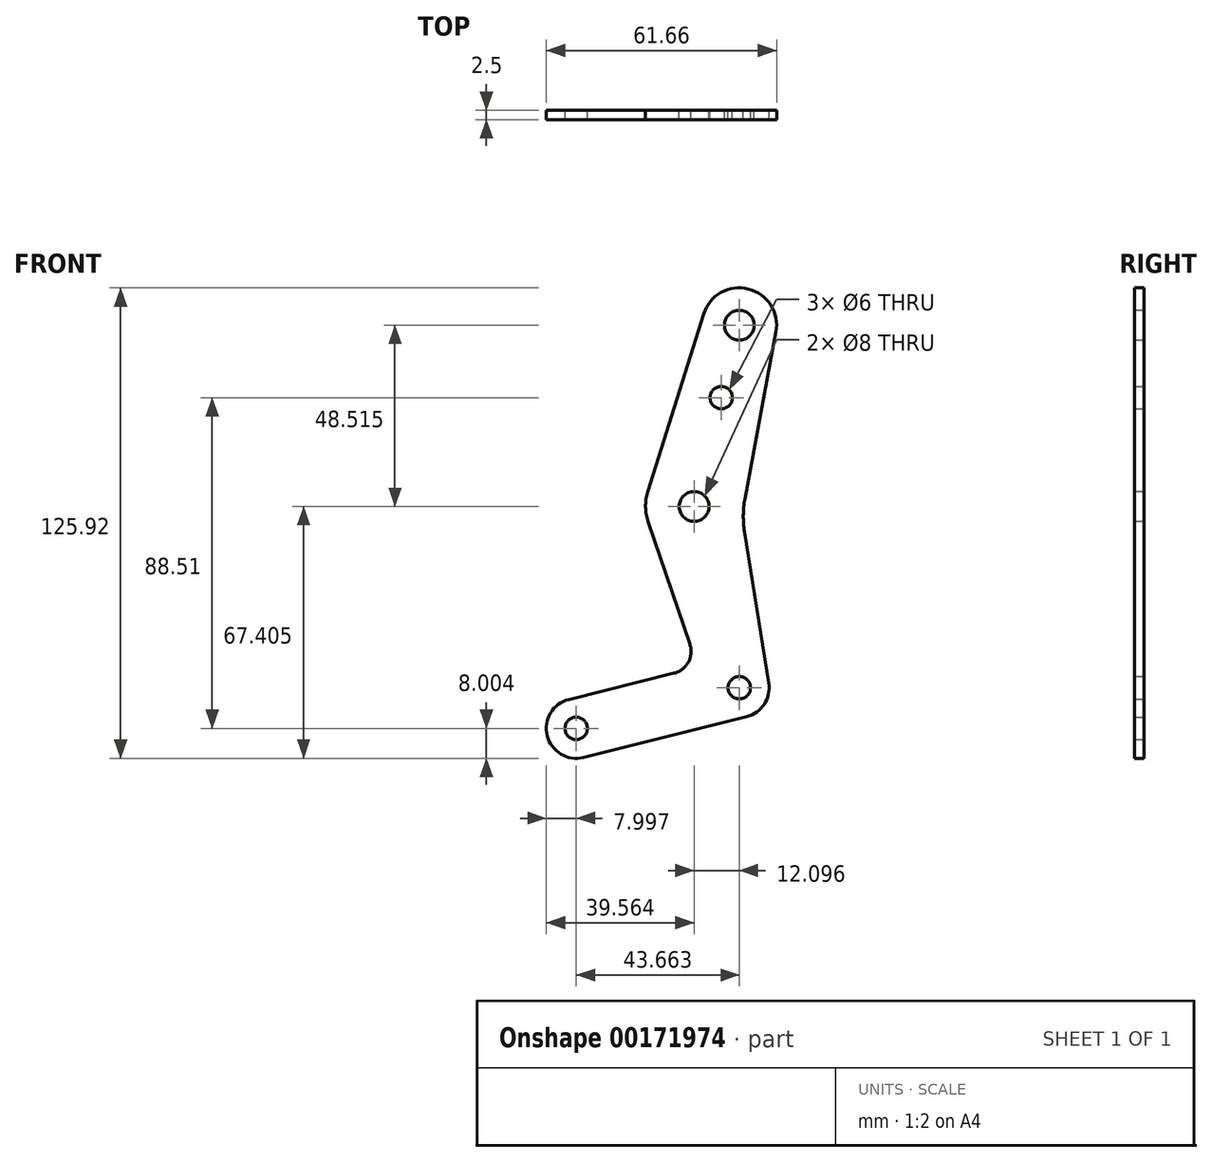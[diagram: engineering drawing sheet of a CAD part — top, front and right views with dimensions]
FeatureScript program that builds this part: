
annotation { "Feature Type Name" : "Feature", "Feature Type Description" : "" }
export const myFeature = defineFeature(function(context is Context, id is Id, definition is map)
    precondition{}
    {
        {
            var Q0;
            Q0=qCreatedBy(makeId("Front.planeOp"),FACE);
            var sketch = newSketch(context, id + "F0", { "sketchPlane" : qUnion([Q0])});
            skLineSegment(sketch, "E0", {"start": v(0, 0) * mm, "end": v(-12.1, -48.51) * mm, "construction": true});
            skLineSegment(sketch, "E1", {"start": v(-12.1, -48.51) * mm, "end": v(0, -97.03) * mm, "construction": true});
            skCircle(sketch, "E2", {"center": v(0, 0) * mm, "radius": 4 * mm});
            skCircle(sketch, "E3", {"center": v(-12.1, -48.51) * mm, "radius": 4 * mm});
            skCircle(sketch, "E4", {"center": v(0, -97.03) * mm, "radius": 3 * mm});
            skCircle(sketch, "E5", {"center": v(-4.84, -19.4) * mm, "radius": 3 * mm});
            skLineSegment(sketch, "E6", {"start": v(0, -97.03) * mm, "end": v(-43.66, -107.92) * mm, "construction": true});
            skCircle(sketch, "E7", {"center": v(-43.66, -107.92) * mm, "radius": 3 * mm});
            skArc(sketch, "E8", {"start": v(-24.5, -44.62) * mm, "mid": v(-25.1, -48.68) * mm, "end": v(-24.4, -52.72) * mm});
            skArc(sketch, "E9", {"start": v(-9.54, 3) * mm, "mid": v(2.42, 9.7) * mm, "end": v(9.83, -1.83) * mm});
            skArc(sketch, "E10", {"start": v(1.94, -104.8) * mm, "mid": v(6.68, -101.44) * mm, "end": v(7.9, -95.76) * mm});
            skArc(sketch, "E11", {"start": v(-45.6, -100.15) * mm, "mid": v(-51.43, -109.85) * mm, "end": v(-41.73, -115.68) * mm});
            skLineSegment(sketch, "E12.0", {"start": v(-17.47, -93.14) * mm, "end": v(-45.6, -100.15) * mm});
            skLineSegment(sketch, "E13.0", {"start": v(1.94, -104.8) * mm, "end": v(-41.73, -115.68) * mm});
            skLineSegment(sketch, "E14", {"start": v(-9.54, 3) * mm, "end": v(-24.5, -44.62) * mm});
            skLineSegment(sketch, "E15.MirrorCS", {"start": v(9.83, -1.83) * mm, "end": v(1.51, -46.46) * mm});
            skLineSegment(sketch, "E16", {"start": v(1.4, -55.35) * mm, "end": v(7.9, -95.76) * mm});
            skPoint(sketch, "E17.visualSharp", {"position": v(0.68, -50.9) * mm});
            skArc(sketch, "E17.filletArc", {"start": v(1.51, -46.46) * mm, "mid": v(1.07, -50.9) * mm, "end": v(1.4, -55.35) * mm});
            skLineSegment(sketch, "E18", {"start": v(-24.4, -52.72) * mm, "end": v(-13.24, -85.38) * mm});
            skPoint(sketch, "E19.visualSharp", {"position": v(-11.13, -91.56) * mm});
            skArc(sketch, "E19.filletArc", {"start": v(-17.47, -93.14) * mm, "mid": v(-13.65, -90.19) * mm, "end": v(-13.24, -85.38) * mm});
            skSolve(sketch);
        }
        {
            var Q0;
            Q0=makeQuery(id+"F0.imprint","IMPRINT",FACE,{"disambiguationData":[TD([[makeQuery(id+"F0.imprint","IMPRINT",EDGE,{"derivedFrom":sQuery(id+"F0.wireOp",EDGE,"E2")}),-1.0]])]});
            extrude(context, id + "F1", {"entities" : qUnion([Q0]), "endBound" : BoundingType.SYMMETRIC, "depth" : 2.5 * mm});
        }
    });
